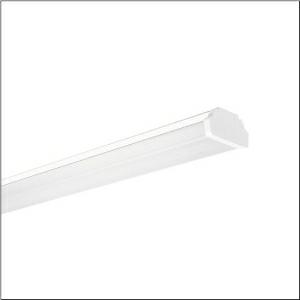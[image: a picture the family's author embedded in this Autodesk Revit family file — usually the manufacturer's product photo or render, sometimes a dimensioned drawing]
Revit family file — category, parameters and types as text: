
# Revit family: dus_r__31_ho_53bd812d2v4120_dd06
name_source: partatom
category: Lighting Fixtures
units: mm (PartAtom-declared; Revit-internal decimal feet)

## family parameters
Cut with Voids When Loaded = No
Host = Face
Light Source = No
Part Type = Normal
Room Calculation Point = No
Round Connector Dimension = Use Diameter
Shared = No

## types (1)
- --- (1 x LED, 12350 lm, 79.5 W, 4000K)
    Apparent Load = 80 VA
    CIE Flux Codes = 47 80 95 92 100
    Color Rendering = 80
    Color Temperature = 4000K
    Default Elevation = 1800 mm
    Description = DUS® 31 HO, luminaire insert, of sheet steel, coil coated, white, length: 1.535mm, width: 81mm, height: 90mm, 5x system unit, system units: 307mm, LED rated luminous flux: 12.350lm, light colour: 840, control gear: DALI 2, control gear: ECG DALI, with plug, 5-pole, with phase selection, mains connection: 220..240V, AC, 50/60Hz, rated input power: 80W, through-wiring accessed according to module size, primary optical cover: cover, of PMMA, light emission: direct distribution, primary light characteristic: symmetric, protection rating (complete): IP20, protection rating (LED compartment): IP50, insulation class (complete): insulation class I (protective earthing), certification: CE, ENEC, VDE, UKCA, impact resistance: IK03, permissible ambient temperature for indoor applications: -25..+30°C, corresponds to IFS (International Featured Standards) requirements for safety and quality in the food industry, reducing of maximum allowable ambient temperature of 5°C with ceiling mounting, packaging unit: 1 piece
    Height = 95 mm
    Lamp = 1 x LED
    Lamp Light Flux = 12350 lm
    Lamp Power = 79.5 W
    Lamp count = 1
    Length = 1535 mm
    Luminous efficacy = 155 lm/W
    Manufacturer = Siteco
    ModVariant = No
    Model = 53BD812D2V4120
    Mounting Place = Ceiling
    Mounting Type = Pendant
    Number of Poles = 1
    OnlyDefault = Yes
    Power Factor = 1
    Product Name = DUS® 31 HO
    Product group = luminaire insert | ceiling pendant
    ProductGroupID = 902
    Protection Class = Protection class I
    Protection Degree = IP 20
    RLX_Detail_Level = 1
    RLX_Emergency_Light_Flux = 0 lm
    RLX_Emergency_Type = 0
    RLX_Emergency_Type_DB = No
    RlxData = <blob elided: 42189 chars, md5=49da830c>
    Socket = socket
    Standby Power = 0 W
    System Light Flux = 12350 lm
    System Power = 80 W
    Type Comments = factory setting: luminous flux: 100 % | dim-lin: 254 | 345 mA
    Type Image = l_1319596.jpg
    URL = http://relux.com
    VarID = @adj_219545
    Voltage = 0 V
    Weight = 0.00 kg
    Width = 81 mm

## geometry (parser evidence)
native form markers: Blend x4, Sweep x11
no freeform markers — native parametric forms only
